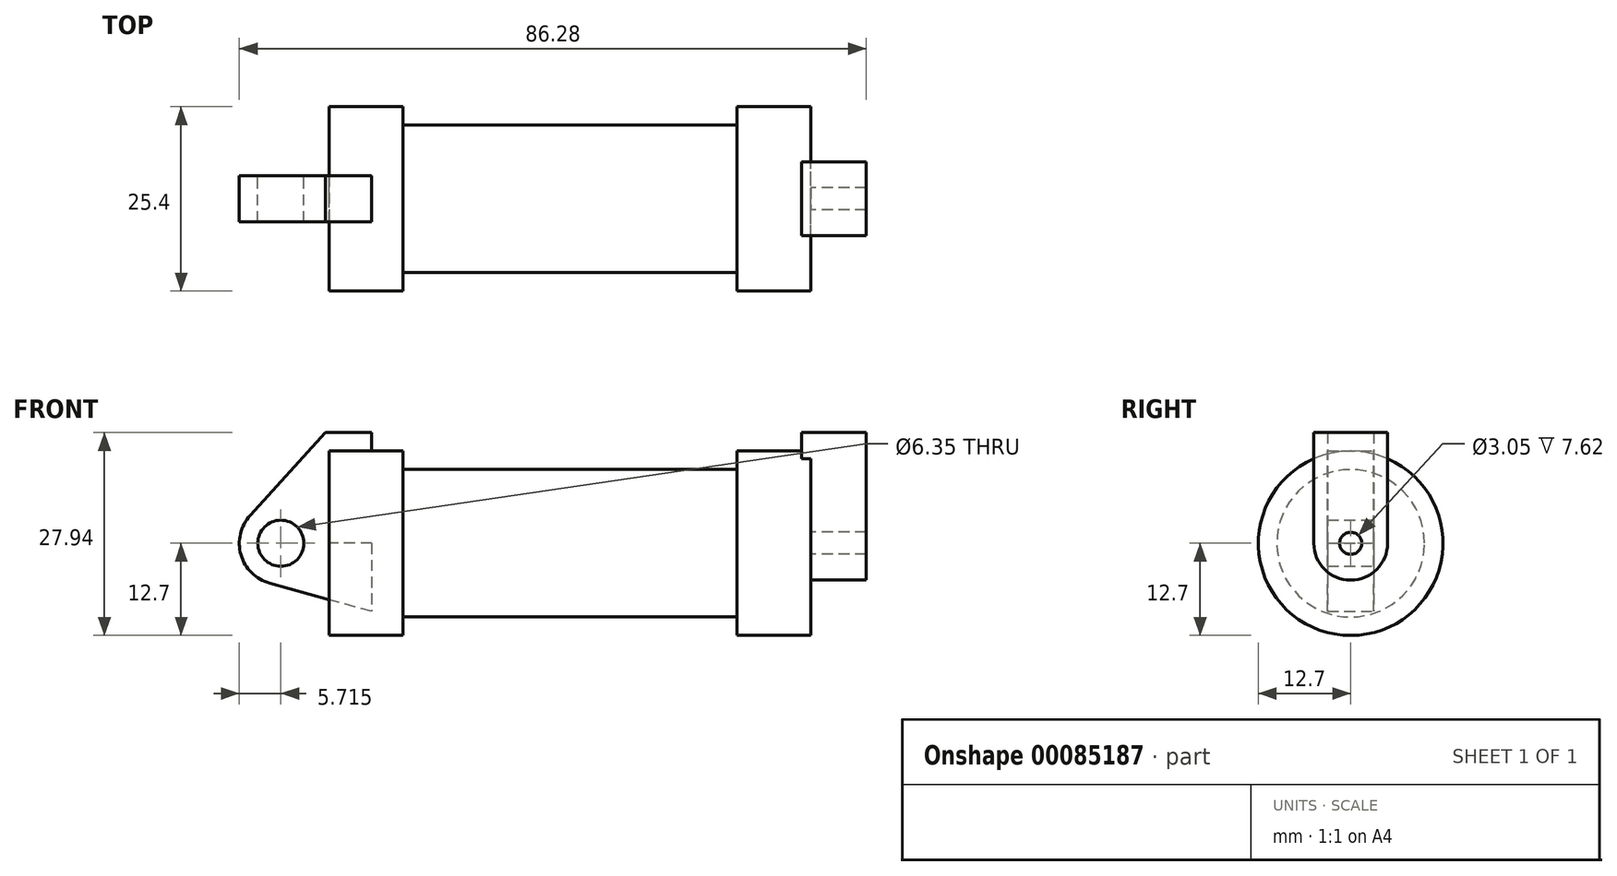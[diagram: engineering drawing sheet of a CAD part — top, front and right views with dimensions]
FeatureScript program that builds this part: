
annotation { "Feature Type Name" : "Feature", "Feature Type Description" : "" }
export const myFeature = defineFeature(function(context is Context, id is Id, definition is map)
    precondition{}
    {
        {
            var Q0;
            Q0=qCreatedBy(makeId("Front.planeOp"),FACE);
            var sketch = newSketch(context, id + "F0", { "sketchPlane" : qUnion([Q0])});
            skLineSegment(sketch, "E0", {"start": v(0, 0) * mm, "end": v(0, 12.7) * mm});
            skLineSegment(sketch, "E1", {"start": v(0, 12.7) * mm, "end": v(10.16, 12.7) * mm});
            skLineSegment(sketch, "E2", {"start": v(10.16, 12.7) * mm, "end": v(10.16, 10.16) * mm});
            skLineSegment(sketch, "E3", {"start": v(10.16, 10.16) * mm, "end": v(56.13, 10.16) * mm});
            skLineSegment(sketch, "E4", {"start": v(56.13, 10.16) * mm, "end": v(56.13, 12.7) * mm});
            skLineSegment(sketch, "E5", {"start": v(56.13, 12.7) * mm, "end": v(66.3, 12.7) * mm});
            skLineSegment(sketch, "E6", {"start": v(66.3, 12.7) * mm, "end": v(66.3, 0) * mm});
            skLineSegment(sketch, "E7", {"start": v(66.3, 0) * mm, "end": v(0, 0) * mm});
            skLineSegment(sketch, "E8", {"start": v(5.84, 15.24) * mm, "end": v(-0.5, 15.24) * mm});
            skLineSegment(sketch, "E9", {"start": v(-0.5, 15.24) * mm, "end": v(-10.88, 3.85) * mm});
            skLineSegment(sketch, "E10", {"start": v(0, 0) * mm, "end": v(-6.65, 0) * mm});
            skCircle(sketch, "E11", {"center": v(-6.65, 0) * mm, "radius": 5.72 * mm});
            skCircle(sketch, "E12", {"center": v(-6.65, 0) * mm, "radius": 3.18 * mm});
            skLineSegment(sketch, "E13", {"start": v(5.84, 15.24) * mm, "end": v(5.84, -9.4) * mm});
            skLineSegment(sketch, "E14", {"start": v(5.84, -9.4) * mm, "end": v(-8.18, -5.5) * mm});
            skSolve(sketch);
        }
        {
            var Q0;
            {var subQ0=sQuery(id+"F0.wireOp",EDGE,"E2");Q0=makeQuery(id+"F0.imprint","IMPRINT",FACE,{"disambiguationData":[TD([[makeQuery(id+"F0.imprint","IMPRINT",EDGE,{"derivedFrom":subQ0}),-1.0]])]});}
            var Q1;
            {var subQ0=sQuery(id+"F0.wireOp",EDGE,"E0");Q1=makeQuery(id+"F0.imprint","IMPRINT",FACE,{"disambiguationData":[TD([[makeQuery(id+"F0.imprint","IMPRINT",EDGE,{"derivedFrom":subQ0}),-1.0]])]});}
            var Q2;
            Q2=sQuery(id+"F0.wireOp",EDGE,"E7");
            revolve(context, id + "F1", {"entities" : qUnion([Q0, Q1]), "axis" : qUnion([Q2]), "revolveType" : RevolveType.FULL});
        }
        {
            var Q0;
            {var subQ3=sQuery(id+"F0.wireOp",EDGE,"E0");Q0=makeQuery(id+"F0.imprint","IMPRINT",FACE,{"disambiguationData":[TD([[makeQuery(id+"F0.imprint","IMPRINT",EDGE,{"derivedFrom":subQ3}),1.0]])]});}
            var Q1;
            {var subQ4=sQuery(id+"F0.wireOp",EDGE,"E12");Q1=makeQuery(id+"F0.imprint","IMPRINT",FACE,{"disambiguationData":[TD([[makeQuery(id+"F0.imprint","IMPRINT",EDGE,{"derivedFrom":subQ4}),-1.0]])]});}
            var Q2;
            {var subQ0=sQuery(id+"F0.wireOp",EDGE,"E14");Q2=makeQuery(id+"F0.imprint","IMPRINT",FACE,{"disambiguationData":[TD([[makeQuery(id+"F0.imprint","IMPRINT",EDGE,{"derivedFrom":subQ0}),-1.0]])]});}
            extrude(context, id + "F2", {"entities" : qUnion([Q0, Q1, Q2]), "endBound" : BoundingType.SYMMETRIC, "depth" : 6.35 * mm});
        }
        {
            var Q0;
            Q0=makeQuery(id+"F1.opRevolve","SWEPT_FACE",FACE,{"disambiguationData":[OSD([sQuery(id+"F0.wireOp",EDGE,"E6")])]});
            var sketch = newSketch(context, id + "F3", { "sketchPlane" : qUnion([Q0])});
            skCircle(sketch, "E15", {"center": v(0, 0) * mm, "radius": 1.52 * mm});
            skCircle(sketch, "E16", {"center": v(0, 0) * mm, "radius": 5.08 * mm});
            skLineSegment(sketch, "E17", {"start": v(-5.08, 0) * mm, "end": v(-5.08, 15.24) * mm});
            skLineSegment(sketch, "E18", {"start": v(5.08, 0) * mm, "end": v(5.08, 15.24) * mm});
            skLineSegment(sketch, "E19", {"start": v(-5.08, 15.24) * mm, "end": v(5.08, 15.24) * mm});
            skSolve(sketch);
        }
        {
            var Q0;
            Q0=qSketchRegion(id+"F3",true);
            extrude(context, id + "F4", {"entities" : qUnion([Q0]), "operationType" : NewBodyOperationType.ADD, "depth" : 7.62 * mm});
        }
        {
            var Q0;
            Q0=makeQuery(id+"F4.opExtrude","CAP_FACE",FACE,{"disambiguationData":[OSD([sQuery(id+"F3.wireOp",EDGE,"E15"),sQuery(id+"F3.wireOp",EDGE,"E16"),sQuery(id+"F3.wireOp",EDGE,"E17"),sQuery(id+"F3.wireOp",EDGE,"E18"),sQuery(id+"F3.wireOp",EDGE,"E19")])],"isStart":true});
            extrude(context, id + "F5", {"entities" : qUnion([Q0]), "operationType" : NewBodyOperationType.ADD, "depth" : 1.27 * mm});
        }
    });
